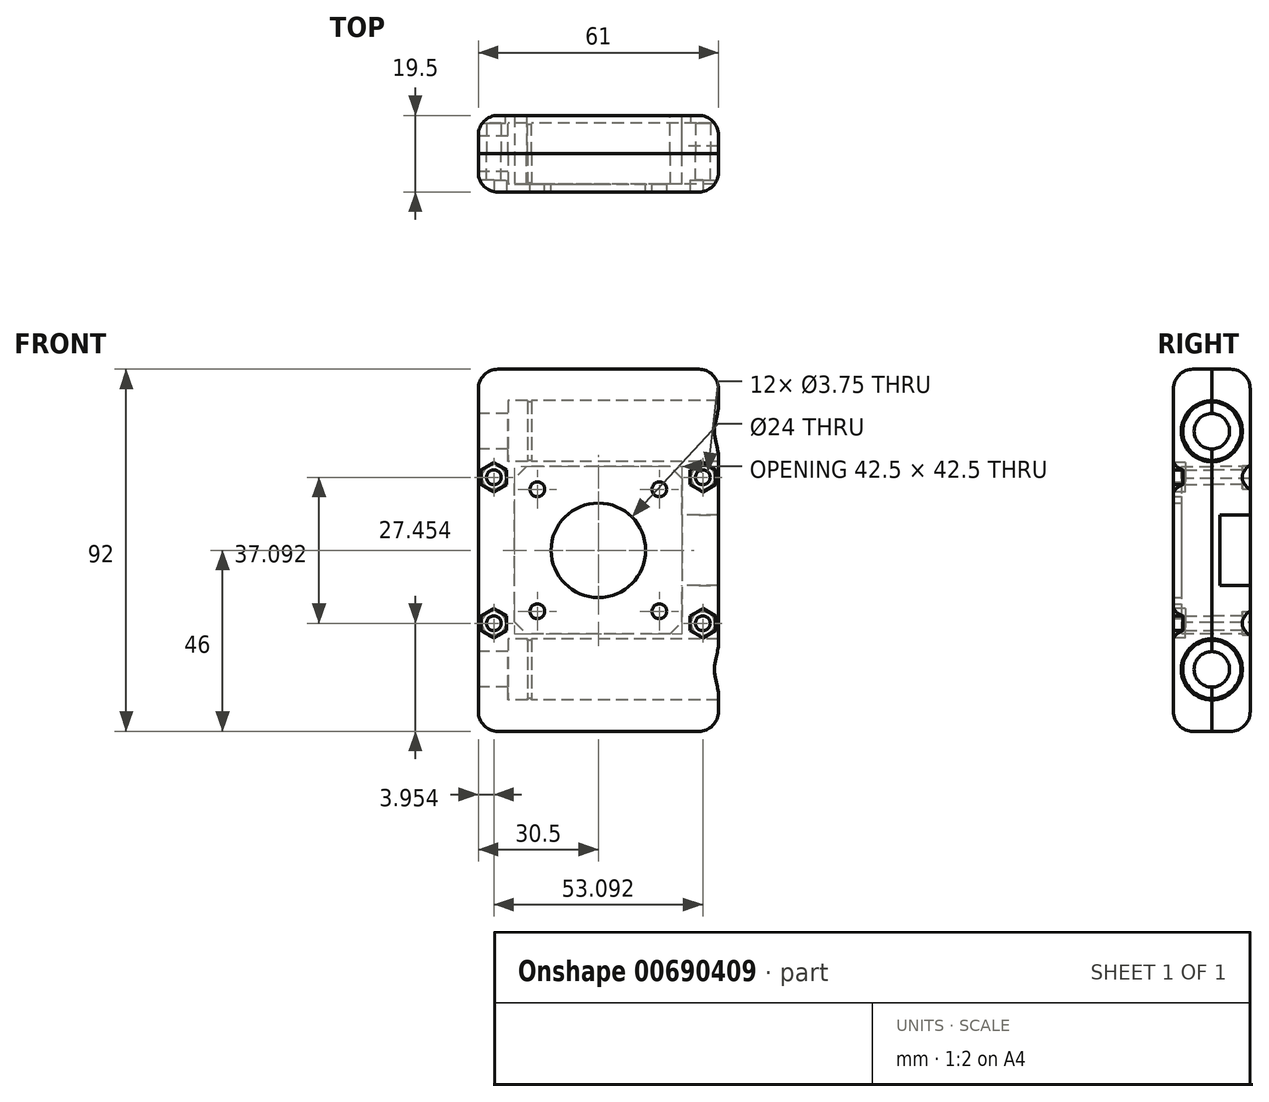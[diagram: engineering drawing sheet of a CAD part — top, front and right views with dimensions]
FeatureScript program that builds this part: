
annotation { "Feature Type Name" : "Feature", "Feature Type Description" : "" }
export const myFeature = defineFeature(function(context is Context, id is Id, definition is map)
    precondition{}
    {
        {
            var Q0;
            Q0=qCreatedBy(makeId("Right.planeOp"),FACE);
            var sketch = newSketch(context, id + "F0", { "sketchPlane" : qUnion([Q0])});
            skLineSegment(sketch, "E0", {"start": v(0, 0) * mm, "end": v(0, 22.5) * mm});
            skArc(sketch, "E1", {"start": v(0, 38) * mm, "mid": v(-7.75, 30.25) * mm, "end": v(0, 22.5) * mm});
            skLineSegment(sketch, "E2", {"start": v(0, 38) * mm, "end": v(0, 46) * mm});
            skLineSegment(sketch, "E3", {"start": v(-9.75, 30.25) * mm, "end": v(-9.75, 0) * mm});
            skLineSegment(sketch, "E4", {"start": v(-7.75, 30.25) * mm, "end": v(-9.75, 30.25) * mm, "construction": true});
            skLineSegment(sketch, "E5", {"start": v(0, 0) * mm, "end": v(-9.75, 0) * mm, "construction": true});
            skLineSegment(sketch, "E6.MirrorCS", {"start": v(0, -38) * mm, "end": v(0, -46) * mm});
            skLineSegment(sketch, "E7.MirrorCS", {"start": v(-7.75, -30.25) * mm, "end": v(-9.75, -30.25) * mm, "construction": true});
            skLineSegment(sketch, "E8.MirrorCS", {"start": v(-9.75, -30.25) * mm, "end": v(-9.75, 0) * mm});
            skLineSegment(sketch, "E9.MirrorCS", {"start": v(0, 0) * mm, "end": v(0, -22.5) * mm});
            skArc(sketch, "E10.MirrorCS", {"start": v(0, -38) * mm, "mid": v(-7.75, -30.25) * mm, "end": v(0, -22.5) * mm});
            skLineSegment(sketch, "E11", {"start": v(-9.75, 30.25) * mm, "end": v(-9.75, 46) * mm});
            skLineSegment(sketch, "E12", {"start": v(-9.75, 46) * mm, "end": v(0, 46) * mm});
            skLineSegment(sketch, "E13", {"start": v(-9.75, -30.25) * mm, "end": v(-9.75, -46) * mm});
            skLineSegment(sketch, "E14", {"start": v(-9.75, -46) * mm, "end": v(0, -46) * mm});
            skSolve(sketch);
        }
        {
            var Q0;
            Q0 = qSketchRegion(id + "F0", true);
            extrude(context, id + "F1", {"entities" : qUnion([Q0]), "endBound" : BoundingType.SYMMETRIC, "depth" : 61 * mm, "offsetDistance" : 25 * mm});
        }
        {
            var Q0;
            Q0=makeQuery(id+"F1.opExtrude","SWEPT_FACE",FACE,{"disambiguationData":[OSD([sQuery(id+"F0.wireOp",EDGE,"E0"),sQuery(id+"F0.wireOp",EDGE,"E9.MirrorCS")])]});
            var sketch = newSketch(context, id + "F2", { "sketchPlane" : qUnion([Q0])});
            skLineSegment(sketch, "E15.bottom", {"start": v(21.25, 21.25) * mm, "end": v(-21.25, 21.25) * mm});
            skLineSegment(sketch, "E15.top", {"start": v(21.25, -21.25) * mm, "end": v(-21.25, -21.25) * mm});
            skLineSegment(sketch, "E15.left", {"start": v(21.25, 21.25) * mm, "end": v(21.25, -21.25) * mm});
            skLineSegment(sketch, "E15.right", {"start": v(-21.25, 21.25) * mm, "end": v(-21.25, -21.25) * mm});
            skPoint(sketch, "E15.middle", {"position": v(0, 0) * mm});
            skSolve(sketch);
        }
        {
            var Q0;
            Q0 = qSketchRegion(id + "F2", true);
            var Q1;
            Q1=makeQuery(id+"F1.opExtrude","SWEPT_FACE",FACE,{"disambiguationData":[OSD([sQuery(id+"F0.wireOp",EDGE,"E3"),sQuery(id+"F0.wireOp",EDGE,"E8.MirrorCS")])]});
            extrude(context, id + "F3", {"entities" : qUnion([Q0]), "operationType" : NewBodyOperationType.REMOVE, "endBound" : BoundingType.UP_TO_SURFACE, "oppositeDirection" : true, "depth" : 25 * mm, "endBoundEntityFace" : qUnion([Q1]), "hasOffset" : true, "offsetDistance" : 2 * mm});
        }
        {
            var Q0;
            Q0=makeQuery(id+"F3.boolean.opBoolean","COPY",FACE,{"derivedFrom":makeQuery(id+"F3.opExtrude","CAP_FACE",FACE,{"disambiguationData":[OSD([sQuery(id+"F2.wireOp",EDGE,"E15.bottom"),sQuery(id+"F2.wireOp",EDGE,"E15.top"),sQuery(id+"F2.wireOp",EDGE,"E15.left"),sQuery(id+"F2.wireOp",EDGE,"E15.right")])],"isStart":false})});
            var sketch = newSketch(context, id + "F4", { "sketchPlane" : qUnion([Q0])});
            skCircle(sketch, "E16", {"center": v(0, 0) * mm, "radius": 12 * mm});
            skLineSegment(sketch, "E17.bottom", {"start": v(15.5, 15.5) * mm, "end": v(-15.5, 15.5) * mm, "construction": true});
            skLineSegment(sketch, "E17.top", {"start": v(15.5, -15.5) * mm, "end": v(-15.5, -15.5) * mm, "construction": true});
            skLineSegment(sketch, "E17.left", {"start": v(15.5, 15.5) * mm, "end": v(15.5, -15.5) * mm, "construction": true});
            skLineSegment(sketch, "E17.right", {"start": v(-15.5, 15.5) * mm, "end": v(-15.5, -15.5) * mm, "construction": true});
            skLineSegment(sketch, "E18", {"start": v(0, 0) * mm, "end": v(0, 15.5) * mm, "construction": true});
            skCircle(sketch, "E19", {"center": v(15.5, 15.5) * mm, "radius": 1.88 * mm});
            skCircle(sketch, "E20", {"center": v(-15.5, 15.5) * mm, "radius": 1.88 * mm});
            skCircle(sketch, "E21", {"center": v(-15.5, -15.5) * mm, "radius": 1.88 * mm});
            skCircle(sketch, "E22", {"center": v(15.5, -15.5) * mm, "radius": 1.88 * mm});
            skSolve(sketch);
        }
        {
            var Q0;
            Q0 = qSketchRegion(id + "F4", true);
            extrude(context, id + "F5", {"entities" : qUnion([Q0]), "operationType" : NewBodyOperationType.REMOVE, "oppositeDirection" : true, "depth" : 25 * mm, "offsetDistance" : 25 * mm});
        }
        {
            var Q0;
            Q0=makeQuery(id+"F1.opExtrude","CAP_FACE",FACE,{"disambiguationData":[OSD([sQuery(id+"F0.wireOp",EDGE,"E0"),sQuery(id+"F0.wireOp",EDGE,"E1"),sQuery(id+"F0.wireOp",EDGE,"E2"),sQuery(id+"F0.wireOp",EDGE,"E3"),sQuery(id+"F0.wireOp",EDGE,"E6.MirrorCS"),sQuery(id+"F0.wireOp",EDGE,"E8.MirrorCS"),sQuery(id+"F0.wireOp",EDGE,"E9.MirrorCS"),sQuery(id+"F0.wireOp",EDGE,"E10.MirrorCS"),sQuery(id+"F0.wireOp",EDGE,"0QtHuTfx-LwfM-BoY6-CbTW-U9HK39Nbpt08"),sQuery(id+"F0.wireOp",EDGE,"6GgkANy2-VNk7-xJdp-5ZtB-LcOKRGDlcmHt")])],"isStart":true});
            var sketch = newSketch(context, id + "F6", { "sketchPlane" : qUnion([Q0])});
            skArc(sketch, "E23.0", {"start": v(0, 38) * mm, "mid": v(7.75, 30.25) * mm, "end": v(0, 22.5) * mm});
            skArc(sketch, "E24", {"start": v(0, 25.75) * mm, "mid": v(4.5, 30.25) * mm, "end": v(0, 34.75) * mm});
            skLineSegment(sketch, "E25", {"start": v(0, 38) * mm, "end": v(0, 34.75) * mm});
            skLineSegment(sketch, "E26", {"start": v(0, 22.5) * mm, "end": v(0, 25.75) * mm});
            skLineSegment(sketch, "E27", {"start": v(0, 0) * mm, "end": v(9.75, 0) * mm, "construction": true});
            skLineSegment(sketch, "E28.MirrorCS", {"start": v(0, -38) * mm, "end": v(0, -34.75) * mm});
            skArc(sketch, "E29.MirrorCS", {"start": v(0, -25.75) * mm, "mid": v(4.5, -30.25) * mm, "end": v(0, -34.75) * mm});
            skArc(sketch, "E30.MirrorCS", {"start": v(0, -38) * mm, "mid": v(7.75, -30.25) * mm, "end": v(0, -22.5) * mm});
            skLineSegment(sketch, "E31.MirrorCS", {"start": v(0, -22.5) * mm, "end": v(0, -25.75) * mm});
            skSolve(sketch);
        }
        {
            var Q0;
            Q0 = qSketchRegion(id + "F6", true);
            extrude(context, id + "F7", {"entities" : qUnion([Q0]), "operationType" : NewBodyOperationType.ADD, "oppositeDirection" : true, "depth" : 7.5 * mm, "offsetDistance" : 25 * mm});
        }
        {
            var Q0;
            Q0=makeQuery(id+"F7.opExtrude","CAP_FACE",FACE,{"disambiguationData":[OSD([sQuery(id+"F6.wireOp",EDGE,"E23.0"),sQuery(id+"F6.wireOp",EDGE,"E24"),sQuery(id+"F6.wireOp",EDGE,"E25"),sQuery(id+"F6.wireOp",EDGE,"E26")])],"isStart":false});
            cPlane(context, id + "F8", {"entities" : qUnion([Q0]), "cplaneType" : CPlaneType.OFFSET, "offset" : 5 * mm, "width" : 150 * mm, "height" : 150 * mm});
        }
        {
            var Q0;
            Q0=qCreatedBy(id+"F8.planeOp",FACE);
            var sketch = newSketch(context, id + "F9", { "sketchPlane" : qUnion([Q0])});
            skArc(sketch, "E32.0", {"start": v(0, 38) * mm, "mid": v(-7.75, 30.25) * mm, "end": v(0, 22.5) * mm});
            skArc(sketch, "E33.0", {"start": v(0, 37.65) * mm, "mid": v(-7.4, 30.25) * mm, "end": v(0, 22.85) * mm});
            skLineSegment(sketch, "E34", {"start": v(0, 38) * mm, "end": v(0, 37.65) * mm});
            skLineSegment(sketch, "E35", {"start": v(0, 22.85) * mm, "end": v(0, 22.5) * mm});
            skLineSegment(sketch, "E36", {"start": v(0, 0) * mm, "end": v(-11.78, 0) * mm, "construction": true});
            skLineSegment(sketch, "E37.MirrorCS", {"start": v(0, -38) * mm, "end": v(0, -37.65) * mm});
            skLineSegment(sketch, "E38.MirrorCS", {"start": v(0, -22.85) * mm, "end": v(0, -22.5) * mm});
            skArc(sketch, "E39.MirrorCS", {"start": v(0, -37.65) * mm, "mid": v(-7.4, -30.25) * mm, "end": v(0, -22.85) * mm});
            skArc(sketch, "E40.MirrorCS", {"start": v(0, -38) * mm, "mid": v(-7.75, -30.25) * mm, "end": v(0, -22.5) * mm});
            skSolve(sketch);
        }
        {
            var Q0;
            Q0 = qSketchRegion(id + "F9", true);
            extrude(context, id + "F10", {"entities" : qUnion([Q0]), "operationType" : NewBodyOperationType.ADD, "depth" : 1 * mm, "offsetDistance" : 25 * mm});
        }
        {
            var Q0;
            Q0=makeQuery(id+"F3.boolean.opBoolean","COPY",EDGE,{"derivedFrom":makeQuery(id+"F3.opExtrude","SWEPT_EDGE",EDGE,{"disambiguationData":[OSD([sQuery(id+"F2.wireOp",EDGE,"E15.bottom"),sQuery(id+"F2.wireOp",EDGE,"E15.left")])]})});
            var Q1;
            Q1=makeQuery(id+"F3.boolean.opBoolean","COPY",EDGE,{"derivedFrom":makeQuery(id+"F3.opExtrude","SWEPT_EDGE",EDGE,{"disambiguationData":[OSD([sQuery(id+"F2.wireOp",EDGE,"E15.bottom"),sQuery(id+"F2.wireOp",EDGE,"E15.right")])]})});
            var Q2;
            Q2=makeQuery(id+"F3.boolean.opBoolean","COPY",EDGE,{"derivedFrom":makeQuery(id+"F3.opExtrude","SWEPT_EDGE",EDGE,{"disambiguationData":[OSD([sQuery(id+"F2.wireOp",EDGE,"E15.top"),sQuery(id+"F2.wireOp",EDGE,"E15.right")])]})});
            var Q3;
            Q3=makeQuery(id+"F3.boolean.opBoolean","COPY",EDGE,{"derivedFrom":makeQuery(id+"F3.opExtrude","SWEPT_EDGE",EDGE,{"disambiguationData":[OSD([sQuery(id+"F2.wireOp",EDGE,"E15.top"),sQuery(id+"F2.wireOp",EDGE,"E15.left")])]})});
            chamfer(context, id + "F11", {"entities" : qUnion([Q0, Q1, Q2, Q3]), "width" : 3 * mm, "tangentPropagation" : true});
        }
        {
            var Q0;
            {var subQ0=sQuery(id+"F6.wireOp",EDGE,"E31.MirrorCS");var subQ1=sQuery(id+"F6.wireOp",EDGE,"E26");Q0=makeQuery(id+"FMOBo1hSkNsZyka_1.1.F7.boolean.opBoolean","MERGE",FACE,{"derivedFrom":[makeQuery(id+"F7.boolean.opBoolean","MERGE",FACE,{"derivedFrom":[makeQuery(id+"F1.opExtrude","SWEPT_FACE",FACE,{"disambiguationData":[OSD([sQuery(id+"F0.wireOp",EDGE,"E0"),sQuery(id+"F0.wireOp",EDGE,"E9.MirrorCS")])]}),makeQuery(id+"F7.opExtrude","SWEPT_FACE",FACE,{"disambiguationData":[OSD([subQ1])]}),makeQuery(id+"F7.opExtrude","SWEPT_FACE",FACE,{"disambiguationData":[OSD([subQ0])]})]}),makeQuery(id+"FMOBo1hSkNsZyka_1.1.F7.opExtrude","SWEPT_FACE",FACE,{"disambiguationData":[OSD([subQ1])]}),makeQuery(id+"FMOBo1hSkNsZyka_1.1.F7.opExtrude","SWEPT_FACE",FACE,{"disambiguationData":[OSD([subQ0])]})]});}
            var sketch = newSketch(context, id + "F12", { "sketchPlane" : qUnion([Q0])});
            skCircle(sketch, "E41", {"center": v(-26.55, 18.55) * mm, "radius": 1.88 * mm});
            skLineSegment(sketch, "E42", {"start": v(-28.42, 18.55) * mm, "end": v(-30.5, 18.55) * mm, "construction": true});
            skLineSegment(sketch, "E43", {"start": v(-26.55, 20.42) * mm, "end": v(-26.55, 22.5) * mm});
            skLineSegment(sketch, "E44", {"start": v(-23.66, 18.78) * mm, "end": v(-20.58, 21.86) * mm, "construction": true});
            skLineSegment(sketch, "E45", {"start": v(-21.8, 20.64) * mm, "end": v(-20.33, 19.17) * mm, "construction": true});
            skLineSegment(sketch, "E46", {"start": v(0, 0) * mm, "end": v(0, 21.25) * mm, "construction": true});
            skLineSegment(sketch, "E47", {"start": v(0, 0) * mm, "end": v(30.5, 0) * mm, "construction": true});
            skCircle(sketch, "E48.MirrorC", {"center": v(26.55, 18.55) * mm, "radius": 1.88 * mm});
            skCircle(sketch, "E49.MirrorC", {"center": v(26.55, -18.55) * mm, "radius": 1.88 * mm});
            skCircle(sketch, "E50.MirrorC", {"center": v(-26.55, -18.55) * mm, "radius": 1.88 * mm});
            skSolve(sketch);
        }
        {
            var Q0;
            Q0 = qSketchRegion(id + "F12", true);
            extrude(context, id + "F13", {"entities" : qUnion([Q0]), "operationType" : NewBodyOperationType.REMOVE, "oppositeDirection" : true, "depth" : 25 * mm, "offsetDistance" : 25 * mm});
        }
        {
            var Q0;
            Q0=makeQuery(id+"F1.opExtrude","SWEPT_EDGE",EDGE,{"disambiguationData":[OSD([sQuery(id+"F0.wireOp",EDGE,"E11"),sQuery(id+"F0.wireOp",EDGE,"E12")])]});
            var Q1;
            Q1=makeQuery(id+"F1.opExtrude","SWEPT_EDGE",EDGE,{"disambiguationData":[OSD([sQuery(id+"F0.wireOp",EDGE,"E13"),sQuery(id+"F0.wireOp",EDGE,"E14")])]});
            fillet(context, id + "F14", {"entities" : qUnion([Q0, Q1]), "radius" : 5 * mm, "tangentPropagation" : true, "allowEdgeOverflow" : false});
        }
        {
            var Q0;
            Q0=makeQuery(id+"F1.opExtrude","SWEPT_BODY",BODY,{"disambiguationData":[OSD([sQuery(id+"F0.wireOp",EDGE,"E0"),sQuery(id+"F0.wireOp",EDGE,"E1"),sQuery(id+"F0.wireOp",EDGE,"E2"),sQuery(id+"F0.wireOp",EDGE,"E3"),sQuery(id+"F0.wireOp",EDGE,"E6.MirrorCS"),sQuery(id+"F0.wireOp",EDGE,"E8.MirrorCS"),sQuery(id+"F0.wireOp",EDGE,"E9.MirrorCS"),sQuery(id+"F0.wireOp",EDGE,"E10.MirrorCS"),sQuery(id+"F0.wireOp",EDGE,"0QtHuTfx-LwfM-BoY6-CbTW-U9HK39Nbpt08"),sQuery(id+"F0.wireOp",EDGE,"6GgkANy2-VNk7-xJdp-5ZtB-LcOKRGDlcmHt")])]});
            var Q1;
            {var subQ0=sQuery(id+"F6.wireOp",EDGE,"E31.MirrorCS");var subQ1=sQuery(id+"F6.wireOp",EDGE,"E26");Q1=makeQuery(id+"FMOBo1hSkNsZyka_1.1.F7.boolean.opBoolean","MERGE",FACE,{"derivedFrom":[makeQuery(id+"F7.boolean.opBoolean","MERGE",FACE,{"derivedFrom":[makeQuery(id+"F1.opExtrude","SWEPT_FACE",FACE,{"disambiguationData":[OSD([sQuery(id+"F0.wireOp",EDGE,"E0"),sQuery(id+"F0.wireOp",EDGE,"E9.MirrorCS")])]}),makeQuery(id+"F7.opExtrude","SWEPT_FACE",FACE,{"disambiguationData":[OSD([subQ1])]}),makeQuery(id+"F7.opExtrude","SWEPT_FACE",FACE,{"disambiguationData":[OSD([subQ0])]})]}),makeQuery(id+"FMOBo1hSkNsZyka_1.1.F7.opExtrude","SWEPT_FACE",FACE,{"disambiguationData":[OSD([subQ1])]}),makeQuery(id+"FMOBo1hSkNsZyka_1.1.F7.opExtrude","SWEPT_FACE",FACE,{"disambiguationData":[OSD([subQ0])]})]});}
            mirror(context, id + "F15", {"entities" : qUnion([Q0]), "mirrorPlane" : qUnion([Q1])});
        }
        {
            var Q0;
            Q0=makeQuery(id+"F15.opPattern","COPY",FACE,{"derivedFrom":makeQuery(id+"F3.boolean.opBoolean","COPY",FACE,{"derivedFrom":makeQuery(id+"F3.opExtrude","CAP_FACE",FACE,{"disambiguationData":[OSD([sQuery(id+"F2.wireOp",EDGE,"E15.bottom"),sQuery(id+"F2.wireOp",EDGE,"E15.top"),sQuery(id+"F2.wireOp",EDGE,"E15.left"),sQuery(id+"F2.wireOp",EDGE,"E15.right")])],"isStart":false})}),"instanceName":"1"});
            var sketch = newSketch(context, id + "F16", { "sketchPlane" : qUnion([Q0])});
            skLineSegment(sketch, "E51.0.0", {"start": v(-18.25, -21.25) * mm, "end": v(18.25, -21.25) * mm});
            skLineSegment(sketch, "E51.0.1", {"start": v(18.25, -21.25) * mm, "end": v(21.25, -18.25) * mm});
            skLineSegment(sketch, "E51.0.2", {"start": v(21.25, -18.25) * mm, "end": v(21.25, 18.25) * mm});
            skLineSegment(sketch, "E51.0.3", {"start": v(18.25, 21.25) * mm, "end": v(21.25, 18.25) * mm});
            skLineSegment(sketch, "E51.0.4", {"start": v(18.25, 21.25) * mm, "end": v(-18.25, 21.25) * mm});
            skLineSegment(sketch, "E51.0.5", {"start": v(-18.25, 21.25) * mm, "end": v(-21.25, 18.25) * mm});
            skLineSegment(sketch, "E51.0.6", {"start": v(-21.25, 18.25) * mm, "end": v(-21.25, -18.25) * mm});
            skLineSegment(sketch, "E51.0.7", {"start": v(-18.25, -21.25) * mm, "end": v(-21.25, -18.25) * mm});
            skSolve(sketch);
        }
        {
            var Q0;
            Q0 = qSketchRegion(id + "F16", true);
            extrude(context, id + "F17", {"entities" : qUnion([Q0]), "operationType" : NewBodyOperationType.REMOVE, "oppositeDirection" : true, "depth" : 25 * mm, "offsetDistance" : 25 * mm});
        }
        {
            var Q0;
            Q0=makeQuery(id+"F1.opExtrude","SWEPT_FACE",FACE,{"disambiguationData":[OSD([sQuery(id+"F0.wireOp",EDGE,"E3"),sQuery(id+"F0.wireOp",EDGE,"E8.MirrorCS"),sQuery(id+"F0.wireOp",EDGE,"E11"),sQuery(id+"F0.wireOp",EDGE,"E13")])]});
            var sketch = newSketch(context, id + "F18", { "sketchPlane" : qUnion([Q0])});
            skCircle(sketch, "E52.cCircle", {"center": v(-26.55, 18.55) * mm, "radius": 3.25 * mm, "construction": true});
            skLineSegment(sketch, "E52.0", {"start": v(-23.3, 20.42) * mm, "end": v(-23.3, 16.67) * mm});
            skLineSegment(sketch, "E52.1", {"start": v(-23.3, 16.67) * mm, "end": v(-26.55, 14.8) * mm});
            skLineSegment(sketch, "E52.2", {"start": v(-26.55, 14.8) * mm, "end": v(-29.8, 16.67) * mm});
            skLineSegment(sketch, "E52.3", {"start": v(-29.8, 16.67) * mm, "end": v(-29.8, 20.42) * mm});
            skLineSegment(sketch, "E52.4", {"start": v(-29.8, 20.42) * mm, "end": v(-26.55, 22.3) * mm});
            skLineSegment(sketch, "E52.5", {"start": v(-26.55, 22.3) * mm, "end": v(-23.3, 20.42) * mm});
            skPoint(sketch, "E52.0.midPoint", {"position": v(-23.3, 18.55) * mm});
            skLineSegment(sketch, "E53", {"start": v(0, 0) * mm, "end": v(0, 8.3) * mm, "construction": true});
            skLineSegment(sketch, "E54", {"start": v(0, 0) * mm, "end": v(-4.56, 0) * mm, "construction": true});
            skLineSegment(sketch, "E55.MirrorCS", {"start": v(26.55, 22.3) * mm, "end": v(23.3, 20.42) * mm});
            skLineSegment(sketch, "E56.MirrorCS", {"start": v(23.3, 20.42) * mm, "end": v(23.3, 16.67) * mm});
            skLineSegment(sketch, "E57.MirrorCS", {"start": v(23.3, 16.67) * mm, "end": v(26.55, 14.8) * mm});
            skLineSegment(sketch, "E58.MirrorCS", {"start": v(26.55, 14.8) * mm, "end": v(29.8, 16.67) * mm});
            skLineSegment(sketch, "E59.MirrorCS", {"start": v(29.8, 16.67) * mm, "end": v(29.8, 20.42) * mm});
            skLineSegment(sketch, "E60.MirrorCS", {"start": v(29.8, 20.42) * mm, "end": v(26.55, 22.3) * mm});
            skLineSegment(sketch, "E61.MirrorCS", {"start": v(29.8, -16.67) * mm, "end": v(29.8, -20.42) * mm});
            skLineSegment(sketch, "E62.MirrorCS", {"start": v(29.8, -20.42) * mm, "end": v(26.55, -22.3) * mm});
            skCircle(sketch, "E63.MirrorC", {"center": v(-26.55, -18.55) * mm, "radius": 3.25 * mm, "construction": true});
            skLineSegment(sketch, "E64.MirrorCS", {"start": v(-23.3, -20.42) * mm, "end": v(-23.3, -16.67) * mm});
            skLineSegment(sketch, "E65.MirrorCS", {"start": v(26.55, -14.8) * mm, "end": v(29.8, -16.67) * mm});
            skLineSegment(sketch, "E66.MirrorCS", {"start": v(-23.3, -16.67) * mm, "end": v(-26.55, -14.8) * mm});
            skPoint(sketch, "E67.MirrorP", {"position": v(-23.3, -18.55) * mm});
            skLineSegment(sketch, "E68.MirrorCS", {"start": v(23.3, -16.67) * mm, "end": v(26.55, -14.8) * mm});
            skLineSegment(sketch, "E69.MirrorCS", {"start": v(23.3, -20.42) * mm, "end": v(23.3, -16.67) * mm});
            skLineSegment(sketch, "E70.MirrorCS", {"start": v(26.55, -22.3) * mm, "end": v(23.3, -20.42) * mm});
            skLineSegment(sketch, "E71.MirrorCS", {"start": v(-26.55, -14.8) * mm, "end": v(-29.8, -16.67) * mm});
            skLineSegment(sketch, "E72.MirrorCS", {"start": v(-29.8, -16.67) * mm, "end": v(-29.8, -20.42) * mm});
            skLineSegment(sketch, "E73.MirrorCS", {"start": v(-26.55, -22.3) * mm, "end": v(-23.3, -20.42) * mm});
            skLineSegment(sketch, "E74.MirrorCS", {"start": v(-29.8, -20.42) * mm, "end": v(-26.55, -22.3) * mm});
            skSolve(sketch);
        }
        {
            var Q0;
            Q0 = qSketchRegion(id + "F18", true);
            extrude(context, id + "F19", {"entities" : qUnion([Q0]), "operationType" : NewBodyOperationType.REMOVE, "oppositeDirection" : true, "depth" : 3 * mm, "offsetDistance" : 25 * mm});
        }
        {
            var Q0;
            Q0=makeQuery(id+"F1.opExtrude","CAP_EDGE",EDGE,{"disambiguationData":[OSD([sQuery(id+"F0.wireOp",EDGE,"E3"),sQuery(id+"F0.wireOp",EDGE,"E8.MirrorCS"),sQuery(id+"F0.wireOp",EDGE,"E11"),sQuery(id+"F0.wireOp",EDGE,"E13")])],"isStart":false});
            var Q1;
            Q1=makeQuery(id+"F1.opExtrude","CAP_EDGE",EDGE,{"disambiguationData":[OSD([sQuery(id+"F0.wireOp",EDGE,"E3"),sQuery(id+"F0.wireOp",EDGE,"E8.MirrorCS"),sQuery(id+"F0.wireOp",EDGE,"E11"),sQuery(id+"F0.wireOp",EDGE,"E13")])],"isStart":true});
            fillet(context, id + "F20", {"entities" : qUnion([Q0, Q1]), "radius" : 5 * mm, "tangentPropagation" : true, "allowEdgeOverflow" : false});
        }
        {
            var Q0;
            Q0=makeQuery(id+"F15.opPattern","COPY",FACE,{"derivedFrom":makeQuery(id+"F1.opExtrude","SWEPT_FACE",FACE,{"disambiguationData":[OSD([sQuery(id+"F0.wireOp",EDGE,"E3"),sQuery(id+"F0.wireOp",EDGE,"E8.MirrorCS"),sQuery(id+"F0.wireOp",EDGE,"E11"),sQuery(id+"F0.wireOp",EDGE,"E13")])]}),"instanceName":"1"});
            var sketch = newSketch(context, id + "F21", { "sketchPlane" : qUnion([Q0])});
            skLineSegment(sketch, "E75.bottom", {"start": v(-30.5, 9) * mm, "end": v(-12, 9) * mm});
            skLineSegment(sketch, "E75.top", {"start": v(-30.5, -9) * mm, "end": v(-12, -9) * mm});
            skLineSegment(sketch, "E75.left", {"start": v(-30.5, 9) * mm, "end": v(-30.5, -9) * mm});
            skLineSegment(sketch, "E75.right", {"start": v(-12, 9) * mm, "end": v(-12, -9) * mm});
            skPoint(sketch, "E75.middle", {"position": v(-21.25, 0) * mm});
            skSolve(sketch);
        }
        {
            var Q0;
            Q0 = qSketchRegion(id + "F21", true);
            var Q1;
            {var subQ0=sQuery(id+"F9.wireOp",EDGE,"E38.MirrorCS");var subQ1=sQuery(id+"F9.wireOp",EDGE,"E35");var subQ2=sQuery(id+"F6.wireOp",EDGE,"E31.MirrorCS");var subQ3=sQuery(id+"F6.wireOp",EDGE,"E26");Q1=makeQuery(id+"F15.opPattern","COPY",FACE,{"derivedFrom":makeQuery(id+"FMOBo1hSkNsZyka_1.1.F10.boolean.opBoolean","MERGE",FACE,{"derivedFrom":[makeQuery(id+"FMOBo1hSkNsZyka_1.1.F7.boolean.opBoolean","MERGE",FACE,{"derivedFrom":[makeQuery(id+"F10.boolean.opBoolean","MERGE",FACE,{"derivedFrom":[makeQuery(id+"F7.boolean.opBoolean","MERGE",FACE,{"derivedFrom":[makeQuery(id+"F1.opExtrude","SWEPT_FACE",FACE,{"disambiguationData":[OSD([sQuery(id+"F0.wireOp",EDGE,"E0"),sQuery(id+"F0.wireOp",EDGE,"E9.MirrorCS")])]}),makeQuery(id+"F7.opExtrude","SWEPT_FACE",FACE,{"disambiguationData":[OSD([subQ3])]}),makeQuery(id+"F7.opExtrude","SWEPT_FACE",FACE,{"disambiguationData":[OSD([subQ2])]})]}),makeQuery(id+"F10.opExtrude","SWEPT_FACE",FACE,{"disambiguationData":[OSD([subQ1])]}),makeQuery(id+"F10.opExtrude","SWEPT_FACE",FACE,{"disambiguationData":[OSD([subQ0])]})]}),makeQuery(id+"FMOBo1hSkNsZyka_1.1.F7.opExtrude","SWEPT_FACE",FACE,{"disambiguationData":[OSD([subQ3])]}),makeQuery(id+"FMOBo1hSkNsZyka_1.1.F7.opExtrude","SWEPT_FACE",FACE,{"disambiguationData":[OSD([subQ2])]})]}),makeQuery(id+"FMOBo1hSkNsZyka_1.1.F10.opExtrude","SWEPT_FACE",FACE,{"disambiguationData":[OSD([subQ1])]}),makeQuery(id+"FMOBo1hSkNsZyka_1.1.F10.opExtrude","SWEPT_FACE",FACE,{"disambiguationData":[OSD([subQ0])]})]}),"instanceName":"1"});}
            extrude(context, id + "F22", {"entities" : qUnion([Q0]), "operationType" : NewBodyOperationType.REMOVE, "endBound" : BoundingType.UP_TO_SURFACE, "oppositeDirection" : true, "depth" : 25 * mm, "endBoundEntityFace" : qUnion([Q1]), "hasOffset" : true, "offsetDistance" : 2 * mm});
        }
        {
            var Q0;
            {var subQ1=sQuery(id+"F0.wireOp",EDGE,"E11");var subQ2=sQuery(id+"F0.wireOp",EDGE,"E13");var subQ3=sQuery(id+"F0.wireOp",EDGE,"E8.MirrorCS");var subQ4=sQuery(id+"F0.wireOp",EDGE,"E3");Q0=makeQuery(id+"F22.boolean.opBoolean","SPLIT",EDGE,{"disambiguationData":[TD([makeQuery(id+"F22.opExtrude","SWEPT_FACE",FACE,{"disambiguationData":[OSD([sQuery(id+"F21.wireOp",EDGE,"E75.bottom")])]})])],"derivedFrom":makeQuery(id+"F15.opPattern","COPY",EDGE,{"derivedFrom":makeQuery(id+"F1.opExtrude","CAP_EDGE",EDGE,{"disambiguationData":[OSD([subQ4,subQ3,subQ1,subQ2])],"isStart":false}),"instanceName":"1"})});}
            var Q1;
            {var subQ1=sQuery(id+"F0.wireOp",EDGE,"E13");var subQ2=sQuery(id+"F0.wireOp",EDGE,"E11");var subQ3=sQuery(id+"F0.wireOp",EDGE,"E8.MirrorCS");var subQ4=sQuery(id+"F0.wireOp",EDGE,"E3");Q1=makeQuery(id+"F22.boolean.opBoolean","SPLIT",EDGE,{"disambiguationData":[TD([makeQuery(id+"F22.opExtrude","SWEPT_FACE",FACE,{"disambiguationData":[OSD([sQuery(id+"F21.wireOp",EDGE,"E75.top")])]})])],"derivedFrom":makeQuery(id+"F15.opPattern","COPY",EDGE,{"derivedFrom":makeQuery(id+"F1.opExtrude","CAP_EDGE",EDGE,{"disambiguationData":[OSD([subQ4,subQ3,subQ2,subQ1])],"isStart":false}),"instanceName":"1"})});}
            var Q2;
            Q2=makeQuery(id+"F15.opPattern","COPY",EDGE,{"derivedFrom":makeQuery(id+"F1.opExtrude","CAP_EDGE",EDGE,{"disambiguationData":[OSD([sQuery(id+"F0.wireOp",EDGE,"E3"),sQuery(id+"F0.wireOp",EDGE,"E8.MirrorCS"),sQuery(id+"F0.wireOp",EDGE,"E11"),sQuery(id+"F0.wireOp",EDGE,"E13")])],"isStart":true}),"instanceName":"1"});
            fillet(context, id + "F23", {"entities" : qUnion([Q0, Q1, Q2]), "radius" : 5 * mm, "tangentPropagation" : true, "allowEdgeOverflow" : false});
        }
        {
            var Q0;
            Q0=makeQuery(id+"F15.opPattern","COPY",FACE,{"derivedFrom":makeQuery(id+"F1.opExtrude","SWEPT_FACE",FACE,{"disambiguationData":[OSD([sQuery(id+"F0.wireOp",EDGE,"E3"),sQuery(id+"F0.wireOp",EDGE,"E8.MirrorCS"),sQuery(id+"F0.wireOp",EDGE,"E11"),sQuery(id+"F0.wireOp",EDGE,"E13")])]}),"instanceName":"1"});
            var sketch = newSketch(context, id + "F24", { "sketchPlane" : qUnion([Q0])});
            skCircle(sketch, "E76", {"center": v(26.55, 18.55) * mm, "radius": 3 * mm});
            skCircle(sketch, "E77", {"center": v(-26.55, 18.55) * mm, "radius": 3 * mm});
            skCircle(sketch, "E78", {"center": v(-26.55, -18.55) * mm, "radius": 3 * mm});
            skCircle(sketch, "E79", {"center": v(26.55, -18.55) * mm, "radius": 3 * mm});
            skSolve(sketch);
        }
        {
            var Q0;
            Q0 = qSketchRegion(id + "F24", true);
            extrude(context, id + "F25", {"entities" : qUnion([Q0]), "operationType" : NewBodyOperationType.REMOVE, "oppositeDirection" : true, "depth" : 2 * mm, "offsetDistance" : 25 * mm});
        }
    });
